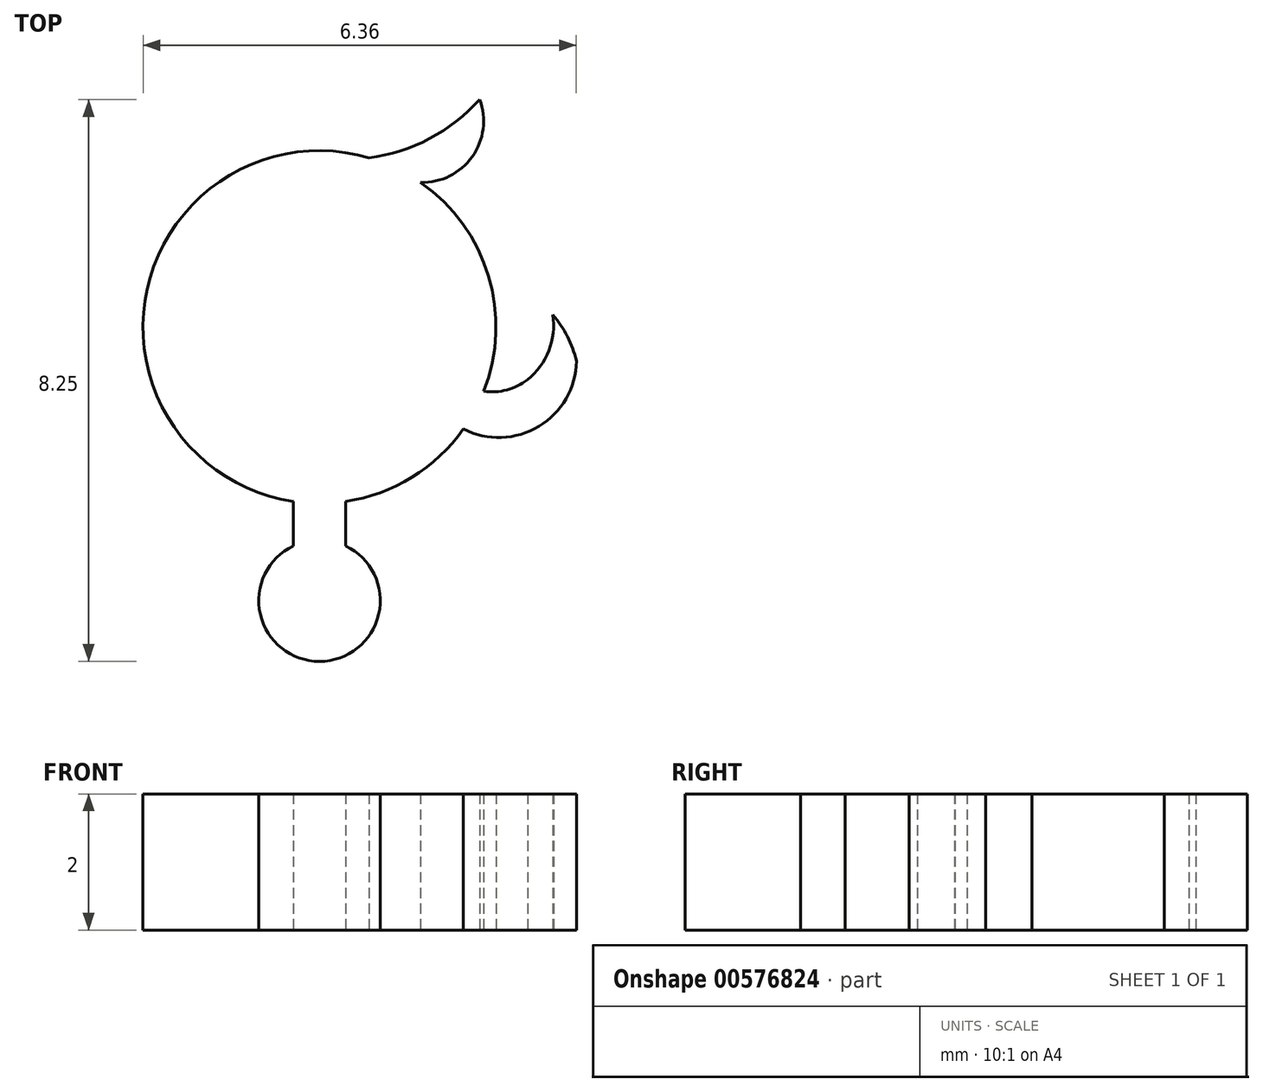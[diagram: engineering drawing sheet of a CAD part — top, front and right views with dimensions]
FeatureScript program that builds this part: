
annotation { "Feature Type Name" : "Feature", "Feature Type Description" : "" }
export const myFeature = defineFeature(function(context is Context, id is Id, definition is map)
    precondition{}
    {
        {
            var Q0;
            Q0=qCreatedBy(makeId("Top.planeOp"),FACE);
            var sketch = newSketch(context, id + "F0", { "sketchPlane" : qUnion([Q0])});
            skArc(sketch, "E0", {"start": v(1.48, 2.12) * mm, "mid": v(2.24, 2.5) * mm, "end": v(2.35, 3.34) * mm});
            skArc(sketch, "E1", {"start": v(0.73, 2.49) * mm, "mid": v(1.62, 2.77) * mm, "end": v(2.35, 3.34) * mm});
            skArc(sketch, "E2", {"start": v(2.11, -1.5) * mm, "mid": v(3.22, -1.46) * mm, "end": v(3.77, -0.5) * mm});
            skArc(sketch, "E3", {"start": v(3.77, -0.5) * mm, "mid": v(3.64, -0.14) * mm, "end": v(3.43, 0.18) * mm});
            skArc(sketch, "E4", {"start": v(2.41, -0.95) * mm, "mid": v(2.75, -0.92) * mm, "end": v(3.06, -0.77) * mm});
            skArc(sketch, "E5", {"start": v(3.06, -0.77) * mm, "mid": v(3.37, -0.35) * mm, "end": v(3.43, 0.18) * mm});
            skArc(sketch, "E6.MirrorCS", {"start": v(-0.73, 2.49) * mm, "mid": v(-1.62, 2.77) * mm, "end": v(-2.35, 3.34) * mm});
            skArc(sketch, "E7.MirrorCS", {"start": v(-1.48, 2.12) * mm, "mid": v(-2.24, 2.5) * mm, "end": v(-2.35, 3.34) * mm});
            skArc(sketch, "E8.MirrorCS", {"start": v(-3.06, -0.77) * mm, "mid": v(-3.37, -0.35) * mm, "end": v(-3.43, 0.18) * mm});
            skArc(sketch, "E9.MirrorCS", {"start": v(-2.41, -0.95) * mm, "mid": v(-2.75, -0.92) * mm, "end": v(-3.06, -0.77) * mm});
            skArc(sketch, "E10.MirrorCS", {"start": v(-2.11, -1.5) * mm, "mid": v(-3.22, -1.46) * mm, "end": v(-3.77, -0.5) * mm});
            skArc(sketch, "E11.MirrorCS", {"start": v(-3.77, -0.5) * mm, "mid": v(-3.64, -0.14) * mm, "end": v(-3.43, 0.18) * mm});
            skArc(sketch, "E12", {"start": v(-2.41, -0.95) * mm, "mid": v(-2.28, -1.23) * mm, "end": v(-2.11, -1.5) * mm});
            skCircle(sketch, "E13", {"center": v(0, 0) * mm, "radius": 2.6 * mm});
            skLineSegment(sketch, "E14", {"start": v(0.38, -2.56) * mm, "end": v(0.38, -3.22) * mm});
            skCircle(sketch, "E15", {"center": v(0, -4.02) * mm, "radius": 0.9 * mm});
            skLineSegment(sketch, "E16.MirrorCS", {"start": v(-0.38, -2.56) * mm, "end": v(-0.38, -3.22) * mm});
            skSolve(sketch);
        }
        {
            var Q0;
            {var subQ0=sQuery(id+"F0.wireOp",EDGE,"E6.MirrorCS");Q0=makeQuery(id+"F0.imprint","IMPRINT",FACE,{"disambiguationData":[TD([[makeQuery(id+"F0.imprint","IMPRINT",EDGE,{"derivedFrom":subQ0}),1.0]])]});}
            var Q1;
            Q1=makeQuery(id+"F0.imprint","IMPRINT",FACE,{"disambiguationData":[TD([[makeQuery(id+"F0.imprint","IMPRINT",EDGE,{"derivedFrom":sQuery(id+"F0.wireOp",EDGE,"E8.MirrorCS")}),1.0]])]});
            var Q2;
            {var subQ1=sQuery(id+"F0.wireOp",EDGE,"E3");Q2=makeQuery(id+"F0.imprint","IMPRINT",FACE,{"disambiguationData":[TD([[makeQuery(id+"F0.imprint","IMPRINT",EDGE,{"derivedFrom":subQ1}),1.0]])]});}
            var Q3;
            {var subQ0=sQuery(id+"F0.wireOp",EDGE,"E15");var subQ1=makeQuery(id+"F0.imprint","INTERSECT",VERTEX,{"derivedFrom":[sQuery(id+"F0.wireOp",EDGE,"E14"),subQ0]});Q3=makeQuery(id+"F0.imprint","IMPRINT",FACE,{"disambiguationData":[TD([[makeQuery(id+"F0.imprint","IMPRINT",EDGE,{"disambiguationData":[TD([[subQ1,-1.0]])],"derivedFrom":subQ0}),1.0]])]});}
            var Q4;
            {var subQ7=sQuery(id+"F0.wireOp",EDGE,"E12");Q4=makeQuery(id+"F0.imprint","IMPRINT",FACE,{"disambiguationData":[TD([[makeQuery(id+"F0.imprint","IMPRINT",EDGE,{"derivedFrom":subQ7}),1.0]])]});}
            var Q5;
            {var subQ0=sQuery(id+"F0.wireOp",EDGE,"E1");Q5=makeQuery(id+"F0.imprint","IMPRINT",FACE,{"disambiguationData":[TD([[makeQuery(id+"F0.imprint","IMPRINT",EDGE,{"derivedFrom":subQ0}),-1.0]])]});}
            var Q6;
            {var subQ0=sQuery(id+"F0.wireOp",EDGE,"E14");Q6=makeQuery(id+"F0.imprint","IMPRINT",FACE,{"disambiguationData":[TD([[makeQuery(id+"F0.imprint","IMPRINT",EDGE,{"derivedFrom":subQ0}),-1.0]])]});}
            var Q7;
            {var subQ0=sQuery(id+"F0.wireOp",EDGE,"E12");Q7=makeQuery(id+"F0.imprint","IMPRINT",FACE,{"disambiguationData":[TD([[makeQuery(id+"F0.imprint","IMPRINT",EDGE,{"derivedFrom":subQ0}),-1.0]])]});}
            extrude(context, id + "F1", {"entities" : qUnion([Q0, Q1, Q2, Q3, Q4, Q5, Q6, Q7]), "depth" : 2 * mm, "offsetDistance" : 25 * mm});
        }
    });
